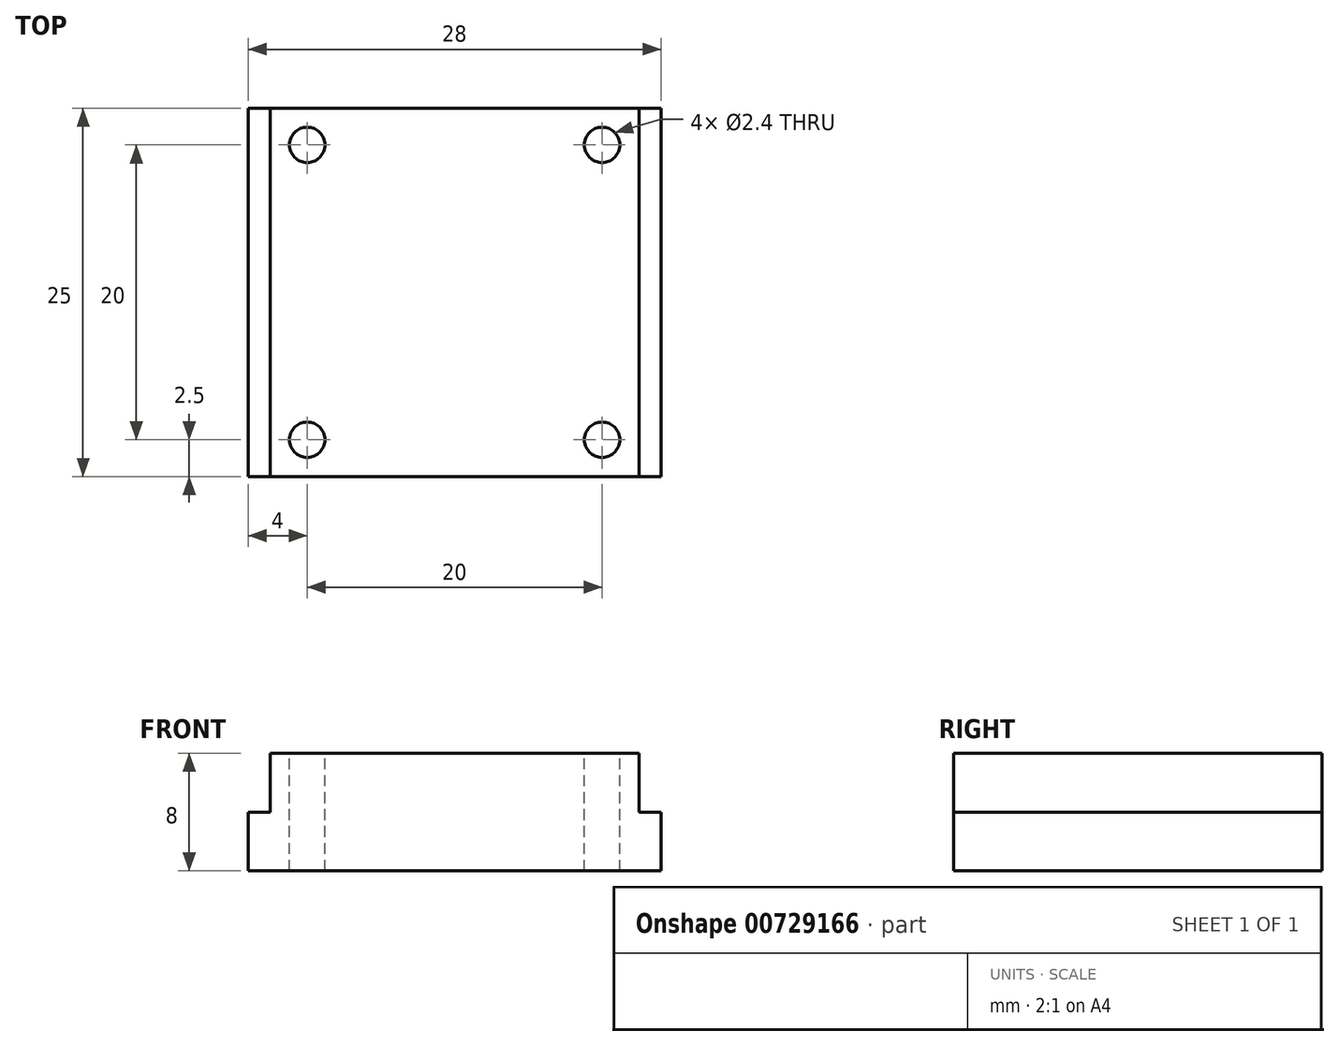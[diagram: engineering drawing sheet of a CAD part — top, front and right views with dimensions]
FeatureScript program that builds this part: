
annotation { "Feature Type Name" : "Feature", "Feature Type Description" : "" }
export const myFeature = defineFeature(function(context is Context, id is Id, definition is map)
    precondition{}
    {
        {
            var Q0;
            Q0=qCreatedBy(makeId("Top.planeOp"),FACE);
            var sketch = newSketch(context, id + "F0", { "sketchPlane" : qUnion([Q0])});
            skLineSegment(sketch, "E0.bottom", {"start": v(14, 12.5) * mm, "end": v(-14, 12.5) * mm});
            skLineSegment(sketch, "E0.top", {"start": v(14, -12.5) * mm, "end": v(-14, -12.5) * mm});
            skLineSegment(sketch, "E0.left", {"start": v(14, 12.5) * mm, "end": v(14, -12.5) * mm});
            skLineSegment(sketch, "E0.right", {"start": v(-14, 12.5) * mm, "end": v(-14, -12.5) * mm});
            skPoint(sketch, "E0.middle", {"position": v(0, 0) * mm});
            skSolve(sketch);
        }
        {
            var Q0;
            Q0=makeQuery(id+"F0.imprint","IMPRINT",FACE,{"disambiguationData":[TD([[makeQuery(id+"F0.imprint","IMPRINT",EDGE,{"derivedFrom":sQuery(id+"F0.wireOp",EDGE,"E0.bottom")}),1.0]])]});
            extrude(context, id + "F1", {"entities" : qUnion([Q0]), "oppositeDirection" : true, "depth" : 4 * mm, "offsetDistance" : 25 * mm});
        }
        {
            var Q0;
            Q0=qCreatedBy(makeId("Top.planeOp"),FACE);
            var sketch = newSketch(context, id + "F2", { "sketchPlane" : qUnion([Q0])});
            skLineSegment(sketch, "E1.bottom", {"start": v(12.5, 12.5) * mm, "end": v(-12.5, 12.5) * mm});
            skLineSegment(sketch, "E1.top", {"start": v(12.5, -12.5) * mm, "end": v(-12.5, -12.5) * mm});
            skLineSegment(sketch, "E1.left", {"start": v(12.5, 12.5) * mm, "end": v(12.5, -12.5) * mm});
            skLineSegment(sketch, "E1.right", {"start": v(-12.5, 12.5) * mm, "end": v(-12.5, -12.5) * mm});
            skPoint(sketch, "E1.middle", {"position": v(0, 0) * mm});
            skSolve(sketch);
        }
        {
            var Q0;
            Q0 = qSketchRegion(id + "F2", true);
            extrude(context, id + "F3", {"entities" : qUnion([Q0]), "operationType" : NewBodyOperationType.ADD, "depth" : 4 * mm, "offsetDistance" : 25 * mm});
        }
        {
            var Q0;
            Q0=makeQuery(id+"F3.opExtrude","CAP_FACE",FACE,{"disambiguationData":[OSD([sQuery(id+"F2.wireOp",EDGE,"E1.bottom"),sQuery(id+"F2.wireOp",EDGE,"E1.top"),sQuery(id+"F2.wireOp",EDGE,"E1.left"),sQuery(id+"F2.wireOp",EDGE,"E1.right")])],"isStart":false});
            var sketch = newSketch(context, id + "F4", { "sketchPlane" : qUnion([Q0])});
            skLineSegment(sketch, "E2.bottom", {"start": v(10, 10) * mm, "end": v(-10, 10) * mm, "construction": true});
            skLineSegment(sketch, "E2.top", {"start": v(10, -10) * mm, "end": v(-10, -10) * mm, "construction": true});
            skLineSegment(sketch, "E2.left", {"start": v(10, 10) * mm, "end": v(10, -10) * mm, "construction": true});
            skLineSegment(sketch, "E2.right", {"start": v(-10, 10) * mm, "end": v(-10, -10) * mm, "construction": true});
            skPoint(sketch, "E2.middle", {"position": v(0, 0) * mm});
            skSolve(sketch);
        }
        {
            var Q0;
            Q0=sQuery(id+"F4.wireOp",VERTEX,"E2.bottom.end");
            var Q1;
            Q1=sQuery(id+"F4.wireOp",VERTEX,"E2.bottom.start");
            var Q2;
            Q2=sQuery(id+"F4.wireOp",VERTEX,"E2.top.start");
            var Q3;
            Q3=sQuery(id+"F4.wireOp",VERTEX,"E2.top.end");
            var Q4;
            Q4=makeQuery(id+"F1.opExtrude","SWEPT_BODY",BODY,{"disambiguationData":[OSD([sQuery(id+"F0.wireOp",EDGE,"E0.bottom"),sQuery(id+"F0.wireOp",EDGE,"E0.top"),sQuery(id+"F0.wireOp",EDGE,"E0.left"),sQuery(id+"F0.wireOp",EDGE,"E0.right")])]});
            hole(context, id + "F5", {"style" : HoleStyle.SIMPLE, "endStyle" : HoleEndStyle.THROUGH, "holeDiameter" : 2.4 * mm, "majorDiameter" : 5 * mm, "isTappedThrough" : true, "tappedDepth" : 12 * mm, "tapClearance" : 3, "locations" : qUnion([Q0, Q1, Q2, Q3]), "scope" : qUnion([Q4])});
        }
    });
